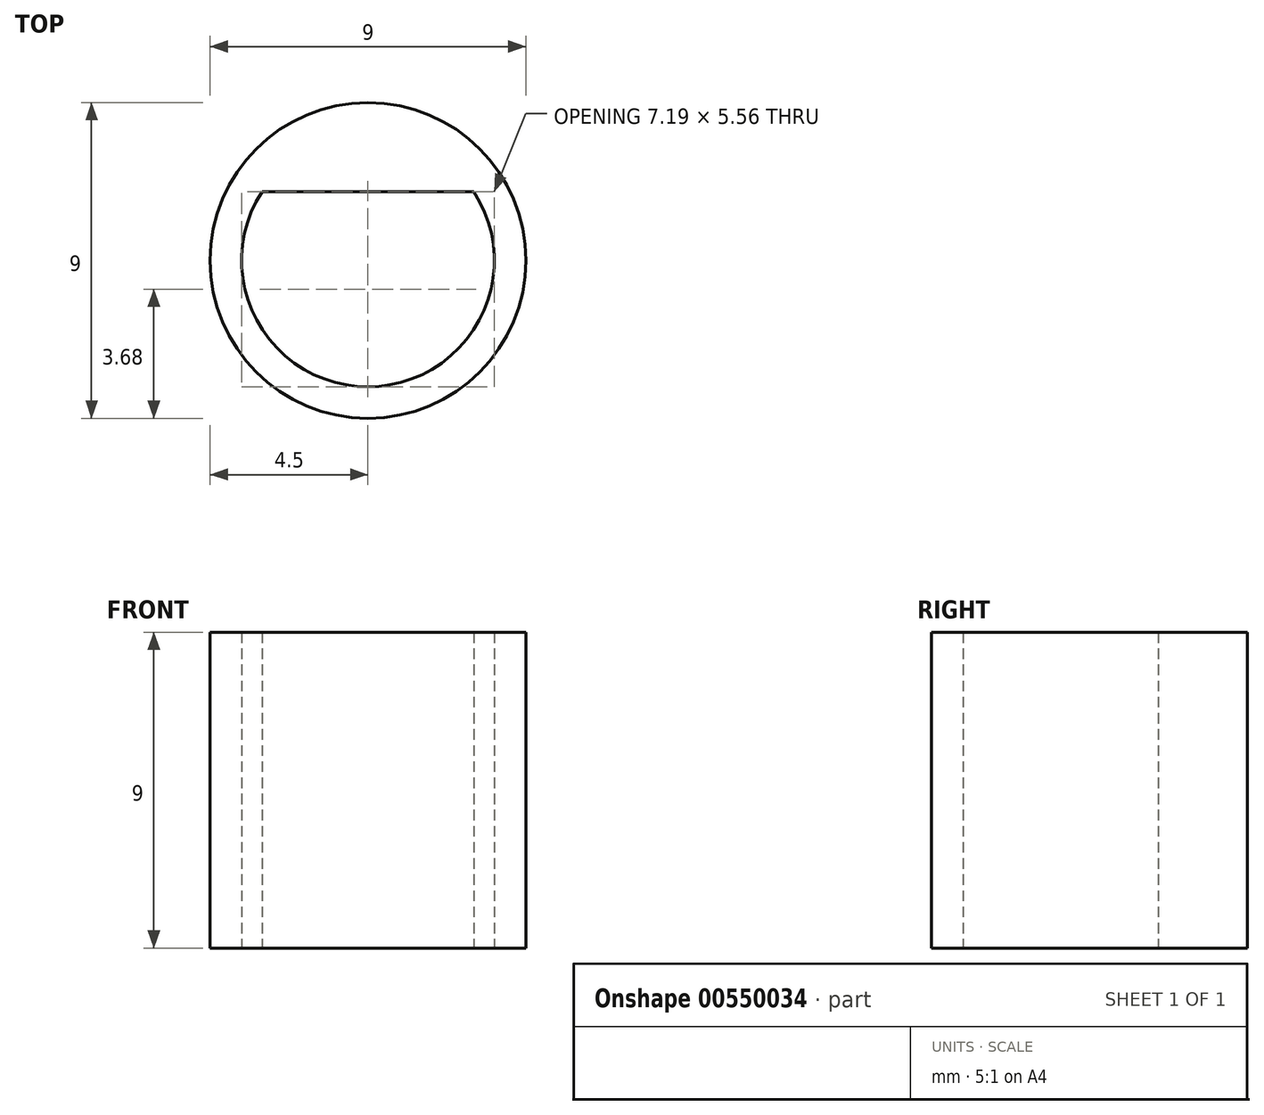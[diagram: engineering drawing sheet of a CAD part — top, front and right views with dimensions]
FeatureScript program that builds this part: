
annotation { "Feature Type Name" : "Feature", "Feature Type Description" : "" }
export const myFeature = defineFeature(function(context is Context, id is Id, definition is map)
    precondition{}
    {
        {
            var Q0;
            Q0=qCreatedBy(makeId("Top.planeOp"),FACE);
            var sketch = newSketch(context, id + "F0", { "sketchPlane" : qUnion([Q0])});
            skArc(sketch, "E0", {"start": v(-3.02, 1.96) * mm, "mid": v(0, -3.6) * mm, "end": v(3.02, 1.96) * mm});
            skCircle(sketch, "E1", {"center": v(0, 0) * mm, "radius": 4.5 * mm});
            skLineSegment(sketch, "E2.top", {"start": v(-3.02, 1.96) * mm, "end": v(3.02, 1.96) * mm});
            skSolve(sketch);
        }
        {
            var Q0;
            Q0 = qSketchRegion(id + "F0", true);
            extrude(context, id + "F1", {"entities" : qUnion([Q0]), "depth" : 4.5 * mm, "offsetDistance" : 25 * mm, "hasSecondDirection" : true, "secondDirectionOppositeDirection" : true, "secondDirectionDepth" : 4.5 * mm});
        }
    });
